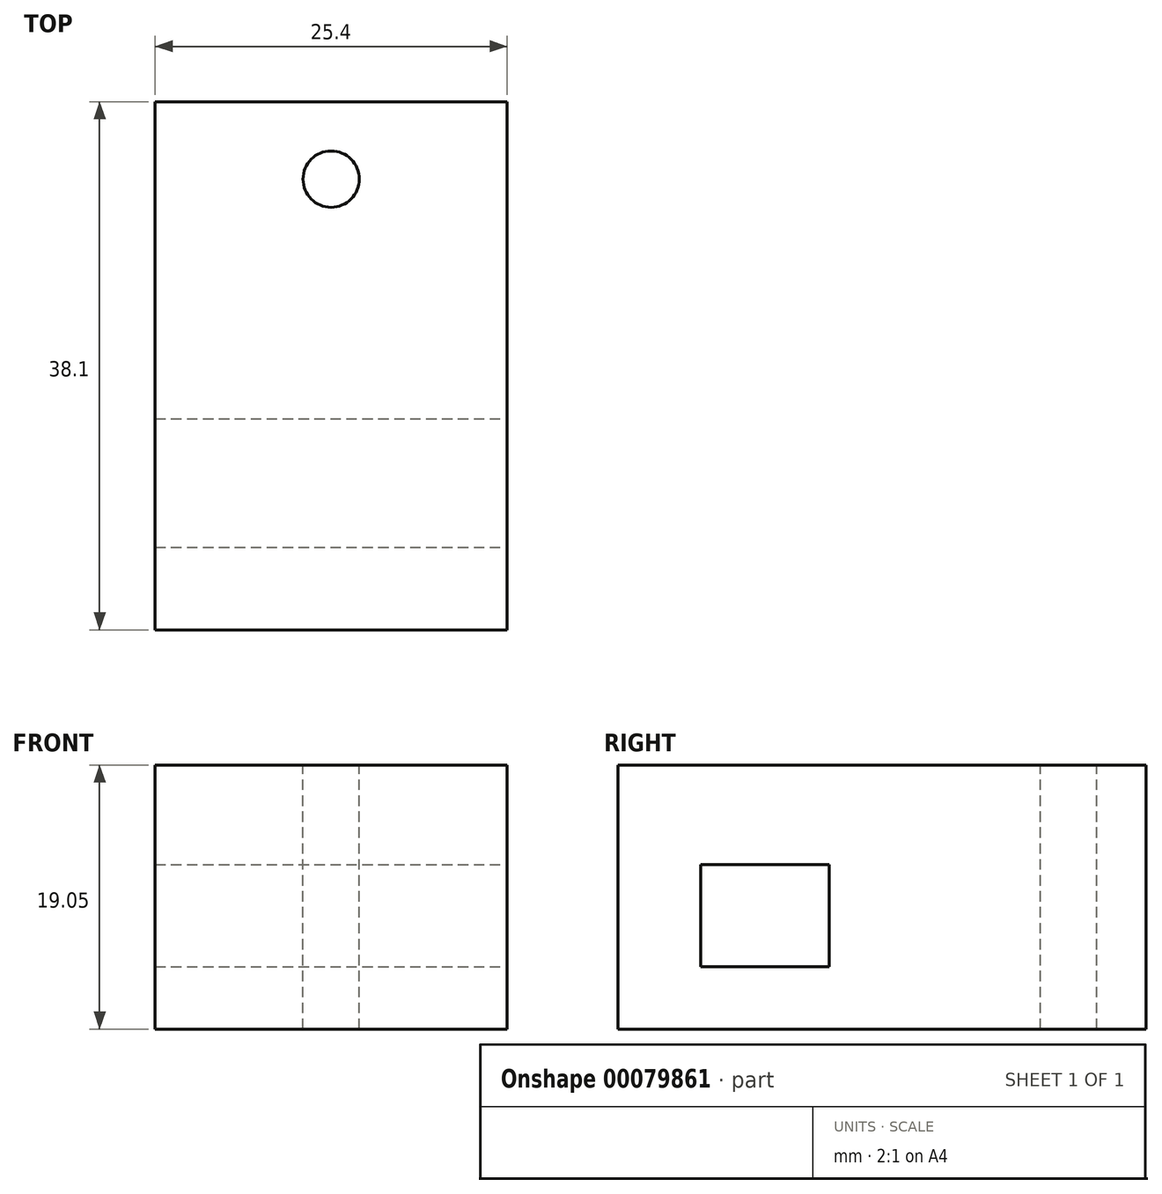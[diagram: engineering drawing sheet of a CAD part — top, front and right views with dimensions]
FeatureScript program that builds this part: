
annotation { "Feature Type Name" : "Feature", "Feature Type Description" : "" }
export const myFeature = defineFeature(function(context is Context, id is Id, definition is map)
    precondition{}
    {
        {
            var Q0;
            Q0=qCreatedBy(makeId("Top.planeOp"),FACE);
            var sketch = newSketch(context, id + "F0", { "sketchPlane" : qUnion([Q0])});
            skLineSegment(sketch, "E0.bottom", {"start": v(-12.7, 12.7) * mm, "end": v(12.7, 12.7) * mm});
            skLineSegment(sketch, "E0.top", {"start": v(-12.7, -25.4) * mm, "end": v(12.7, -25.4) * mm});
            skLineSegment(sketch, "E0.left", {"start": v(-12.7, 12.7) * mm, "end": v(-12.7, -25.4) * mm});
            skLineSegment(sketch, "E0.right", {"start": v(12.7, 12.7) * mm, "end": v(12.7, -25.4) * mm});
            skSolve(sketch);
        }
        {
            var Q0;
            Q0=makeQuery(id+"F0.imprint","IMPRINT",FACE,{"disambiguationData":[TD([[makeQuery(id+"F0.imprint","IMPRINT",EDGE,{"derivedFrom":sQuery(id+"F0.wireOp",EDGE,"E0.bottom")}),-1.0]])]});
            extrude(context, id + "F1", {"entities" : qUnion([Q0]), "depth" : 19.05 * mm});
        }
        {
            var Q0;
            Q0=makeQuery(id+"F1.opExtrude","CAP_FACE",FACE,{"disambiguationData":[OSD([sQuery(id+"F0.wireOp",EDGE,"E0.bottom"),sQuery(id+"F0.wireOp",EDGE,"E0.top"),sQuery(id+"F0.wireOp",EDGE,"E0.left"),sQuery(id+"F0.wireOp",EDGE,"E0.right")])],"isStart":false});
            var sketch = newSketch(context, id + "F2", { "sketchPlane" : qUnion([Q0])});
            skCircle(sketch, "E1", {"center": v(0, 7.11) * mm, "radius": 2.03 * mm});
            skSolve(sketch);
        }
        {
            var Q0;
            Q0=makeQuery(id+"F2.imprint","IMPRINT",FACE,{"disambiguationData":[TD([[makeQuery(id+"F2.imprint","IMPRINT",EDGE,{"derivedFrom":sQuery(id+"F2.wireOp",EDGE,"E1")}),1.0]])]});
            extrude(context, id + "F3", {"entities" : qUnion([Q0]), "operationType" : NewBodyOperationType.REMOVE, "oppositeDirection" : true, "depth" : 25.4 * mm});
        }
        {
            var Q0;
            Q0=makeQuery(id+"F1.opExtrude","SWEPT_FACE",FACE,{"disambiguationData":[OSD([sQuery(id+"F0.wireOp",EDGE,"E0.right")])]});
            var sketch = newSketch(context, id + "F4", { "sketchPlane" : qUnion([Q0])});
            skLineSegment(sketch, "E2.bottom", {"start": v(-19.43, 11.86) * mm, "end": v(-10.16, 11.86) * mm});
            skLineSegment(sketch, "E2.top", {"start": v(-19.43, 4.5) * mm, "end": v(-10.16, 4.5) * mm});
            skLineSegment(sketch, "E2.left", {"start": v(-19.43, 11.86) * mm, "end": v(-19.43, 4.5) * mm});
            skLineSegment(sketch, "E2.right", {"start": v(-10.16, 11.86) * mm, "end": v(-10.16, 4.5) * mm});
            skSolve(sketch);
        }
        {
            var Q0;
            Q0=makeQuery(id+"F4.imprint","IMPRINT",FACE,{"disambiguationData":[TD([[makeQuery(id+"F4.imprint","IMPRINT",EDGE,{"derivedFrom":sQuery(id+"F4.wireOp",EDGE,"E2.bottom")}),-1.0]])]});
            extrude(context, id + "F5", {"entities" : qUnion([Q0]), "operationType" : NewBodyOperationType.REMOVE, "oppositeDirection" : true, "depth" : 25.4 * mm});
        }
    });
